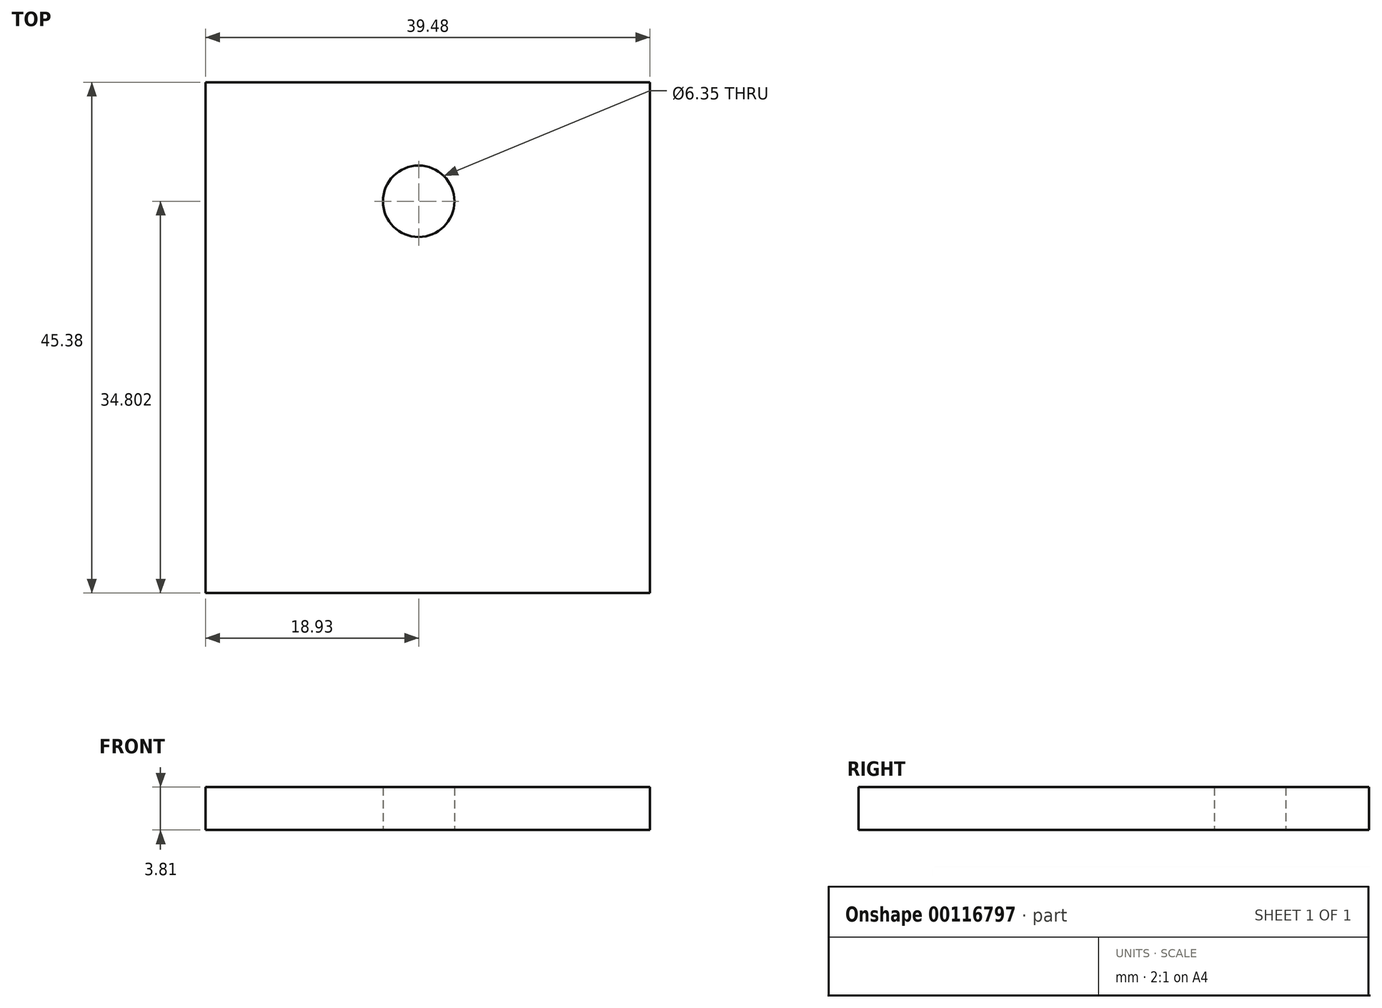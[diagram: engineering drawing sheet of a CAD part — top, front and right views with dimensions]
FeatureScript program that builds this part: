
annotation { "Feature Type Name" : "Feature", "Feature Type Description" : "" }
export const myFeature = defineFeature(function(context is Context, id is Id, definition is map)
    precondition{}
    {
        {
            var Q0;
            Q0=qCreatedBy(makeId("Top.planeOp"),FACE);
            var sketch = newSketch(context, id + "F0", { "sketchPlane" : qUnion([Q0])});
            skLineSegment(sketch, "E0.bottom", {"start": v(20.55, 33.98) * mm, "end": v(-18.93, 33.98) * mm});
            skLineSegment(sketch, "E0.top", {"start": v(20.55, -11.4) * mm, "end": v(-18.93, -11.4) * mm});
            skLineSegment(sketch, "E0.left", {"start": v(20.55, 33.98) * mm, "end": v(20.55, -11.4) * mm});
            skLineSegment(sketch, "E0.right", {"start": v(-18.93, 33.98) * mm, "end": v(-18.93, -11.4) * mm});
            skSolve(sketch);
        }
        {
            var Q0;
            Q0 = qSketchRegion(id + "F0", true);
            extrude(context, id + "F1", {"entities" : qUnion([Q0]), "depth" : 3.8 * mm});
        }
        {
            var Q0;
            Q0=makeQuery(id+"F1.opExtrude","CAP_FACE",FACE,{"disambiguationData":[OSD([sQuery(id+"F0.wireOp",EDGE,"E0.bottom"),sQuery(id+"F0.wireOp",EDGE,"E0.top"),sQuery(id+"F0.wireOp",EDGE,"E0.left"),sQuery(id+"F0.wireOp",EDGE,"E0.right")])],"isStart":true});
            var sketch = newSketch(context, id + "F2", { "sketchPlane" : qUnion([Q0])});
            skPoint(sketch, "E1", {"position": v(0, -23.4) * mm});
            skSolve(sketch);
        }
        {
            var Q0;
            Q0=sQuery(id+"F2.wireOp",VERTEX,"E1");
            var Q1;
            Q1=makeQuery(id+"F1.opExtrude","SWEPT_BODY",BODY,{"disambiguationData":[OSD([sQuery(id+"F0.wireOp",EDGE,"E0.bottom"),sQuery(id+"F0.wireOp",EDGE,"E0.top"),sQuery(id+"F0.wireOp",EDGE,"E0.left"),sQuery(id+"F0.wireOp",EDGE,"E0.right")])]});
            hole(context, id + "F3", {"style" : HoleStyle.SIMPLE, "endStyle" : HoleEndStyle.THROUGH, "holeDiameter" : 6.35 * mm, "locations" : qUnion([Q0]), "scope" : qUnion([Q1]), "isTappedThrough" : true});
        }
    });
